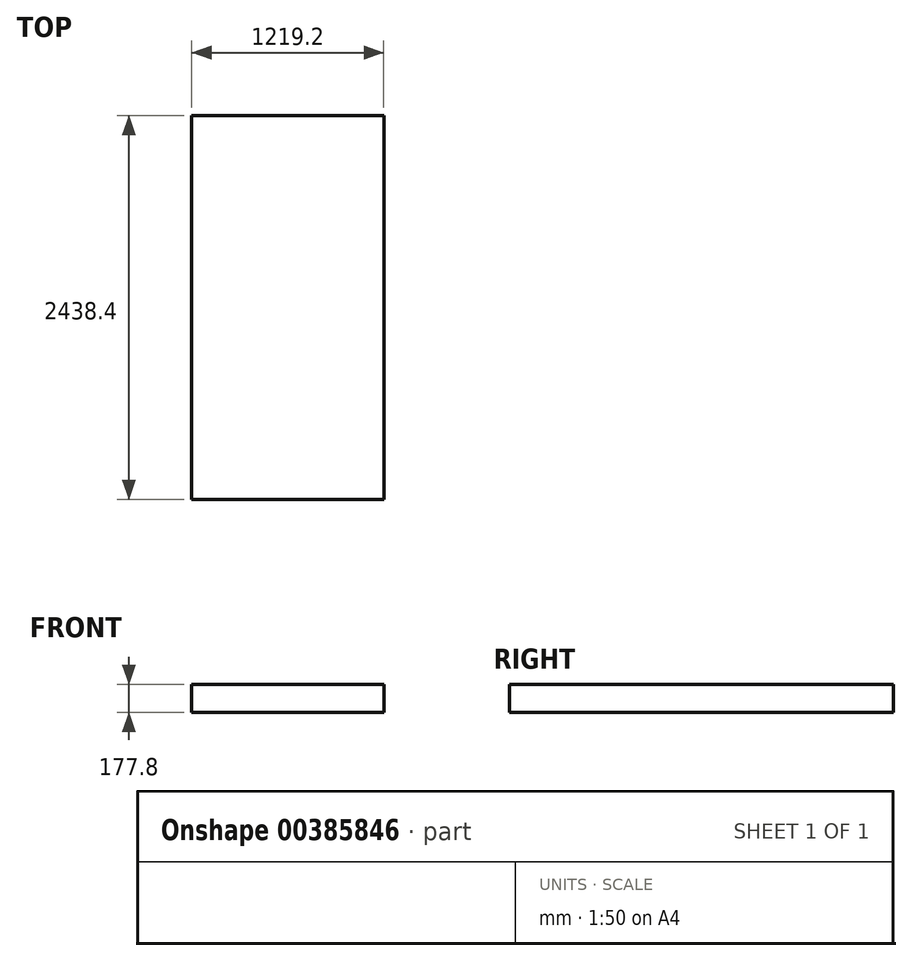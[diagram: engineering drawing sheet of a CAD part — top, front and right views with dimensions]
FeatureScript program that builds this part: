
annotation { "Feature Type Name" : "Feature", "Feature Type Description" : "" }
export const myFeature = defineFeature(function(context is Context, id is Id, definition is map)
    precondition{}
    {
        {
            var Q0;
            Q0=qCreatedBy(makeId("Top.planeOp"),FACE);
            var sketch = newSketch(context, id + "F0", { "sketchPlane" : qUnion([Q0])});
            skLineSegment(sketch, "E0.bottom", {"start": v(1065.96, 2.93) * mm, "end": v(-153.24, 2.93) * mm});
            skLineSegment(sketch, "E0.top", {"start": v(1065.96, 2441.33) * mm, "end": v(-153.24, 2441.33) * mm});
            skLineSegment(sketch, "E0.left", {"start": v(1065.96, 2.93) * mm, "end": v(1065.96, 2441.33) * mm});
            skLineSegment(sketch, "E0.right", {"start": v(-153.24, 2.93) * mm, "end": v(-153.24, 2441.33) * mm});
            skPoint(sketch, "E0.middle", {"position": v(456.36, 1222.13) * mm});
            skSolve(sketch);
        }
        {
            var Q0;
            Q0 = qSketchRegion(id + "F0", true);
            var Q1;
            Q1=makeQuery(id+"F0.imprint","IMPRINT",FACE,{"disambiguationData":[TD([[makeQuery(id+"F0.imprint","IMPRINT",EDGE,{"derivedFrom":sQuery(id+"F0.wireOp",EDGE,"E0.bottom")}),-1.0]])]});
            extrude(context, id + "F1", {"entities" : qUnion([Q0, Q1]), "depth" : 177.8 * mm});
        }
    });
